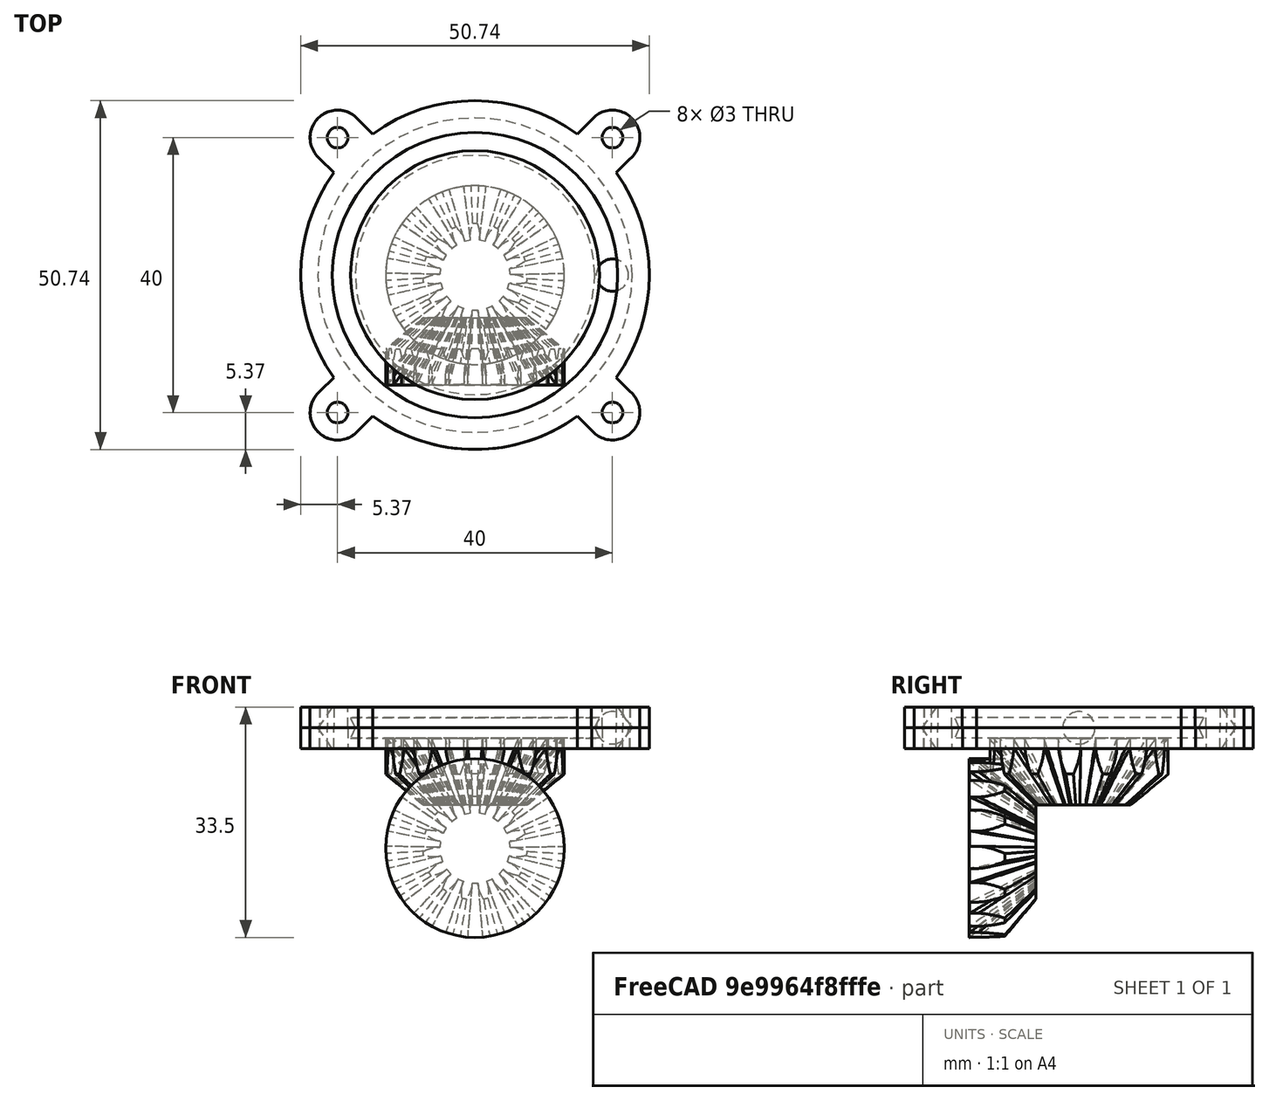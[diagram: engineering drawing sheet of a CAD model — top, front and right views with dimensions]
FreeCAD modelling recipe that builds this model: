
FCSTD DOCUMENT  (FreeCAD 0.16RUnknown)
Label: FrontTurntable
License: CreativeCommons Attribution-NonCommercial
LicenseURL: http://creativecommons.org/licenses/by-nc/4.0/
objects: Sketcher::SketchObject×5, Part::FeaturePython×2, Part::Feature×2, PartDesign::Revolution×2, Mesh::Feature×1, Part::Cylinder×1, Part::MultiCommon×1, Part::Sphere×1, PartDesign::Pad×1, Part::MultiFuse×1
note: 19 computed .brp shape members not serialized (recipe doc carries the construction recipe); baked Part::Feature solids carry a one-line shape summary decoded from their .brp

FEATURE [Sketcher::SketchObject] Sketch
  sketch-geometry (1):
    g0: Circle CenterX=0 CenterY=0 CenterZ=0 NormalX=0 NormalY=0 NormalZ=1 Radius=38.9036
  constraints (1):
    c: Coincident(g0,g-1)
FEATURE [Mesh::Feature] ParallaxServo
  Placement = pos=(-9.85,-60,0) rot=(-1,0,0;1.5708rad)
FEATURE [Part::FeaturePython] BevelGear  # WARN: FeaturePython — macro-defined, semantics opaque (R4)
  Placement = pos=(0,0,0) rot=(1,0,0;1.5708rad)
  backlash = 0
  clearance = 0.1
  height = 10
  m = 1.5
  numpoints = 6
  pitch_angle = 45
  pressure_angle = 20
  teeth = 15
FEATURE [Part::Cylinder] Cylinder
  Angle = 360
  Height = 10
  Placement = pos=(0,-6,0) rot=(1,0,0;1.5708rad)
  Radius = 13
FEATURE [Part::MultiCommon] Common
  Shapes = -> [BevelGear,Cylinder]
FEATURE [Part::Feature] Common001  label="Common"
  Placement = pos=(0,0,0) rot=(-1,0,0;1.5708rad)
  shape: bbox 39.21 x 39 x 10 mm, 93 faces (baked)
FEATURE [Sketcher::SketchObject] Sketch002
  sketch-geometry (4):
    g0: LineSegment StartX=-37.751 StartY=-52.9363 StartZ=0 EndX=37.249 EndY=-52.9363 EndZ=0
    g1: LineSegment StartX=37.249 StartY=-52.9363 StartZ=0 EndX=37.249 EndY=-2.93628 EndZ=0
    g2: LineSegment StartX=37.249 StartY=-2.93628 StartZ=0 EndX=-37.751 EndY=-2.93628 EndZ=0
    g3: LineSegment StartX=-37.751 StartY=-2.93628 StartZ=0 EndX=-37.751 EndY=-52.9363 EndZ=0
  constraints (10):
    c: Coincident(g0,g1)
    c: Coincident(g1,g2)
    c: Coincident(g2,g3)
    c: Coincident(g3,g0)
    c: Horizontal(g0)
    c: Horizontal(g2)
    c: Vertical(g1)
    c: Vertical(g3)
    c: DistanceY(g1,g1) = 50
    c: DistanceX(g2,g2) = 75
FEATURE [Sketcher::SketchObject] Sketch003
  Placement = pos=(0,0,16) rot=(0.57735,0.57735,0.57735;2.0944rad)
  sketch-geometry (9):
    g0: LineSegment StartX=0 StartY=0 StartZ=0 EndX=18.1065 EndY=0 EndZ=0
    g1: LineSegment StartX=18.1065 StartY=3 StartZ=0 EndX=0 EndY=3 EndZ=0
    g2: LineSegment StartX=0 StartY=3 StartZ=0 EndX=0 EndY=0 EndZ=0
    g3: Circle [constr] CenterX=20 CenterY=1.5 CenterZ=0 NormalX=0 NormalY=0 NormalZ=1 Radius=2.25
    g4: LineSegment [constr] StartX=20 StartY=1.5 StartZ=0 EndX=0 EndY=1.5 EndZ=0
    g5: LineSegment StartX=18.1065 StartY=3 StartZ=0 EndX=17.4071 EndY=1.5 EndZ=0
    g6: LineSegment StartX=17.4071 StartY=1.5 StartZ=0 EndX=18.1065 EndY=0 EndZ=0
    g7: LineSegment [constr] StartX=18.1065 StartY=3 StartZ=0 EndX=18.1065 EndY=0 EndZ=0
    g8: Circle [constr] CenterX=20 CenterY=1.5 CenterZ=0 NormalX=0 NormalY=0 NormalZ=1 Radius=2.35
  constraints (23):
    c: Coincident(g-1,g0)
    c: PointOnObject(g1,g-2)
    c: Coincident(g1,g2)
    c: Coincident(g2,g0)
    c: PointOnObject(g0,g-1)
    c: Horizontal(g1)
    c: Radius(g3) = 2.25
    c: PointOnObject(g4,g2)
    c: Symmetric(g1,g-1,g4)
    c: DistanceY(g2,g2) = 3
    c: Coincident(g4,g3)
    c: Coincident(g5,g1)
    c: PointOnObject(g5,g4)
    c: Coincident(g6,g5)
    c: Coincident(g6,g0)
    c: Coincident(g7,g1)
    c: Coincident(g7,g0)
    c: Vertical(g7)
    c: Angle(g6,g5) = 2.26893
    c: Coincident(g8,g3)
    c: Radius(g8) = 2.35
    c: Tangent(g8,g5)
    c: DistanceX(g-1,g3) = 20
FEATURE [PartDesign::Revolution] Revolution
  Angle = 360
  Axis = (0,0,1)
  Base = (0,0,16)
  Placement = pos=(0,0,16) rot=(0.57735,0.57735,0.57735;2.0944rad)
  ReferenceAxis = -> Sketch003 [V_Axis]
  Reversed = true
  Sketch = -> Sketch003
FEATURE [Sketcher::SketchObject] Sketch004
  Placement = pos=(0,0,16) rot=(0.57735,0.57735,0.57735;2.0944rad)
  sketch-geometry (5):
    g0: Circle [constr] CenterX=20 CenterY=1.5 CenterZ=0 NormalX=0 NormalY=0 NormalZ=1 Radius=2.35
    g1: LineSegment StartX=20.7682 StartY=-1.5 StartZ=0 EndX=22.8688 EndY=1.5 EndZ=0
    g2: LineSegment StartX=22.8688 StartY=1.5 StartZ=0 EndX=25.3688 EndY=1.5 EndZ=0
    g3: LineSegment StartX=20.7682 StartY=-1.5 StartZ=0 EndX=25.3688 EndY=-1.5 EndZ=0
    g4: LineSegment StartX=25.3688 StartY=-1.5 StartZ=0 EndX=25.3688 EndY=1.5 EndZ=0
  constraints (15):
    c: Radius(g0) = 2.35
    c: DistanceX(g0) = 20
    c: DistanceY(g0) = 1.5
    c: Coincident(g1,g2)
    c: Horizontal(g2)
    c: Horizontal(g3)
    c: Coincident(g3,g4)
    c: Coincident(g4,g2)
    c: Vertical(g4)
    c: DistanceY(g-1,g2) = 1.5
    c: Tangent(g0,g1)
    c: DistanceX(g2,g2) = 2.5
    c: Coincident(g1,g3)
    c: Angle(g3,g1) = 0.959931
    c: DistanceY(g4,g4) = 3
FEATURE [PartDesign::Revolution] Revolution001
  Angle = 360
  Axis = (0,0,1)
  Base = (0,0,16)
  Placement = pos=(0,0,16) rot=(0.57735,0.57735,0.57735;2.0944rad)
  ReferenceAxis = -> Sketch004 [V_Axis]
  Reversed = true
  Sketch = -> Sketch004
FEATURE [Part::Sphere] Sphere
  Angle1 = -90
  Angle2 = 90
  Angle3 = 360
  Placement = pos=(20,0,17.5) rot=(0,0,1;0rad)
  Radius = 2.35
FEATURE [Sketcher::SketchObject] Sketch005
  Placement = pos=(0,0,14.5) rot=(0,0,1;0rad)
  sketch-geometry (6):
    g0: Circle CenterX=20 CenterY=20 CenterZ=0 NormalX=0 NormalY=0 NormalZ=1 Radius=1.5
    g1: ArcOfCircle CenterX=0 CenterY=0 CenterZ=0 NormalX=0 NormalY=0 NormalZ=1 Radius=25 StartAngle=0.625164 EndAngle=0.945315
    g2: LineSegment [constr] StartX=20 StartY=20 StartZ=0 EndX=0 EndY=0 EndZ=0
    g3: ArcOfCircle CenterX=20 CenterY=20 CenterZ=0 NormalX=0 NormalY=0 NormalZ=1 Radius=4 StartAngle=5.42273 EndAngle=8.73713
    g4: LineSegment StartX=14.6372 StartY=20.267 StartZ=0 EndX=16.909 EndY=22.5389 EndZ=0
    g5: LineSegment StartX=20.2717 StartY=14.6308 StartZ=0 EndX=22.6084 EndY=16.9674 EndZ=0
  constraints (15):
    c: Radius(g0) = 1.5
    c: Coincident(g1,g-1)
    c: Radius(g1) = 25
    c: Coincident(g2,g0)
    c: Coincident(g2,g-1)
    c: Angle(g-1,g2) = 0.785398
    c: DistanceX(g-1,g0) = 20
    c: Coincident(g3,g0)
    c: Coincident(g4,g1)
    c: Coincident(g4,g3)
    c: Coincident(g5,g1)
    c: Coincident(g5,g3)
    c: Parallel(g5,g4)
    c: Parallel(g4,g2)
    c: Radius(g3) = 4
FEATURE [PartDesign::Pad] Pad  label="MountingJoint"
  Length = 3
  Length2 = 100
  Placement = pos=(0,0,14.5) rot=(0,0,1;0rad)
  Sketch = -> Sketch005
  Type = 0
FEATURE [Part::FeaturePython] Array  # Draft array (typed FeaturePython)
  Angle = 360
  ArrayType = 1
  Axis = (0,0,1)
  Base = -> Pad
  Center = (0,0,1)
  Fuse = false
  IntervalAxis = (0,0,0)
  IntervalX = (1,0,0)
  IntervalY = (0,1,0)
  IntervalZ = (0,0,0)
  NumberPolar = 4
  NumberX = 1
  NumberY = 1
  NumberZ = 1
FEATURE [Part::MultiFuse] Fusion
  Shapes = -> [Array,Revolution001]
FEATURE [Part::Feature] Fusion001  label="Fusion"
  Placement = pos=(0,0,35) rot=(1,0,0;3.14159rad)
  shape: bbox 50.74 x 50.74 x 3 mm, 23 faces (baked)
